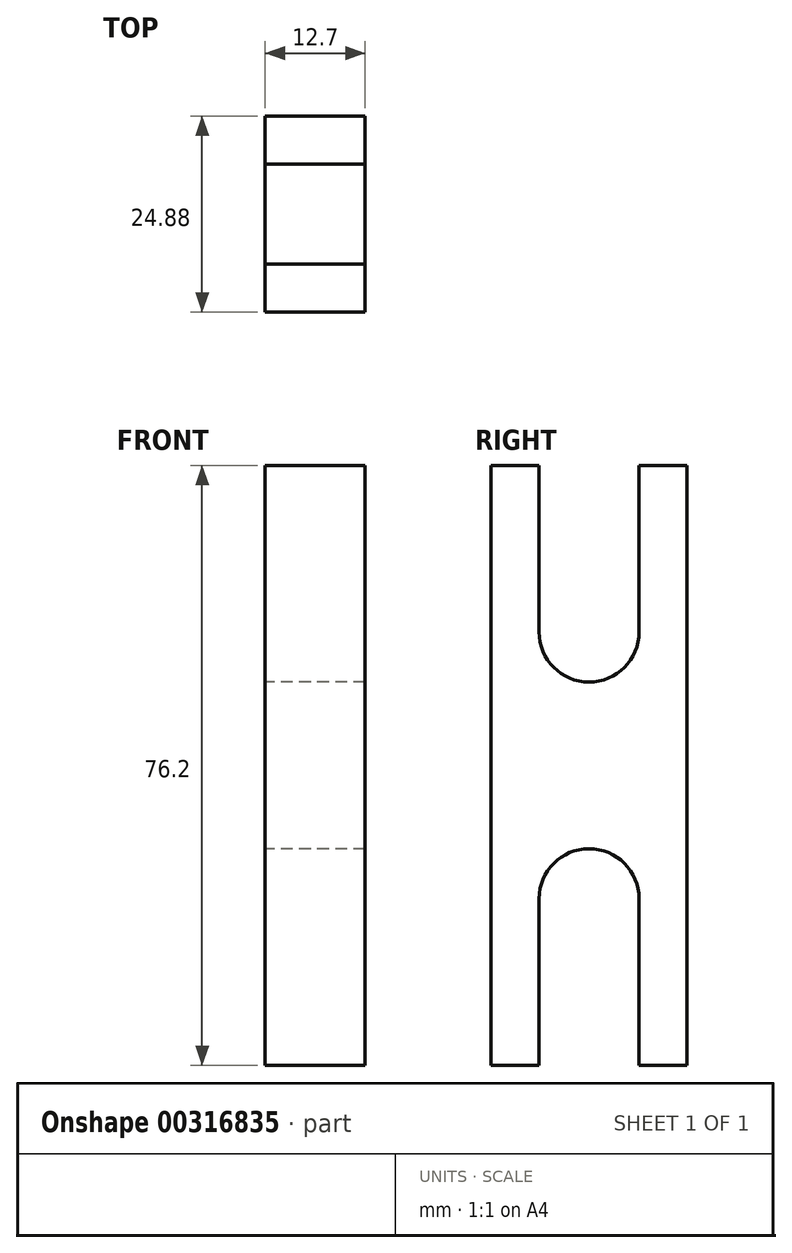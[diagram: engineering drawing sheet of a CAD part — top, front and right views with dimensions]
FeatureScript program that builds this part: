
annotation { "Feature Type Name" : "Feature", "Feature Type Description" : "" }
export const myFeature = defineFeature(function(context is Context, id is Id, definition is map)
    precondition{}
    {
        {
            var Q0;
            Q0=qCreatedBy(makeId("Right.planeOp"),FACE);
            var sketch = newSketch(context, id + "F0", { "sketchPlane" : qUnion([Q0])});
            skLineSegment(sketch, "E0", {"start": v(0, -24.6) * mm, "end": v(0, 51.6) * mm, "construction": true});
            skLineSegment(sketch, "E1", {"start": v(12.44, -24.6) * mm, "end": v(12.44, 51.6) * mm});
            skLineSegment(sketch, "E2", {"start": v(-12.44, 51.6) * mm, "end": v(-12.44, -24.6) * mm});
            skLineSegment(sketch, "E3", {"start": v(-12.44, 51.6) * mm, "end": v(-6.35, 51.6) * mm});
            skLineSegment(sketch, "E4", {"start": v(12.44, 51.6) * mm, "end": v(6.35, 51.6) * mm});
            skLineSegment(sketch, "E5", {"start": v(12.44, -24.6) * mm, "end": v(6.35, -24.6) * mm});
            skLineSegment(sketch, "E6", {"start": v(-12.44, -24.6) * mm, "end": v(-6.35, -24.6) * mm});
            skLineSegment(sketch, "E7", {"start": v(-6.35, 51.6) * mm, "end": v(-6.35, 30.43) * mm});
            skLineSegment(sketch, "E8", {"start": v(6.35, 51.6) * mm, "end": v(6.35, 30.43) * mm});
            skLineSegment(sketch, "E9", {"start": v(6.35, -24.6) * mm, "end": v(6.35, -3.44) * mm});
            skLineSegment(sketch, "E10", {"start": v(-6.35, -24.6) * mm, "end": v(-6.35, -3.44) * mm});
            skArc(sketch, "E11", {"start": v(-6.35, 30.43) * mm, "mid": v(0, 24.08) * mm, "end": v(6.35, 30.43) * mm});
            skArc(sketch, "E12", {"start": v(6.35, -3.44) * mm, "mid": v(0, 2.91) * mm, "end": v(-6.35, -3.44) * mm});
            skSolve(sketch);
        }
        {
            var Q0;
            Q0=makeQuery(id+"F0.imprint","IMPRINT",FACE,{"disambiguationData":[TD([[makeQuery(id+"F0.imprint","IMPRINT",EDGE,{"derivedFrom":sQuery(id+"F0.wireOp",EDGE,"E1")}),1.0]])]});
            extrude(context, id + "F1", {"entities" : qUnion([Q0]), "depth" : 12.7 * mm});
        }
    });
